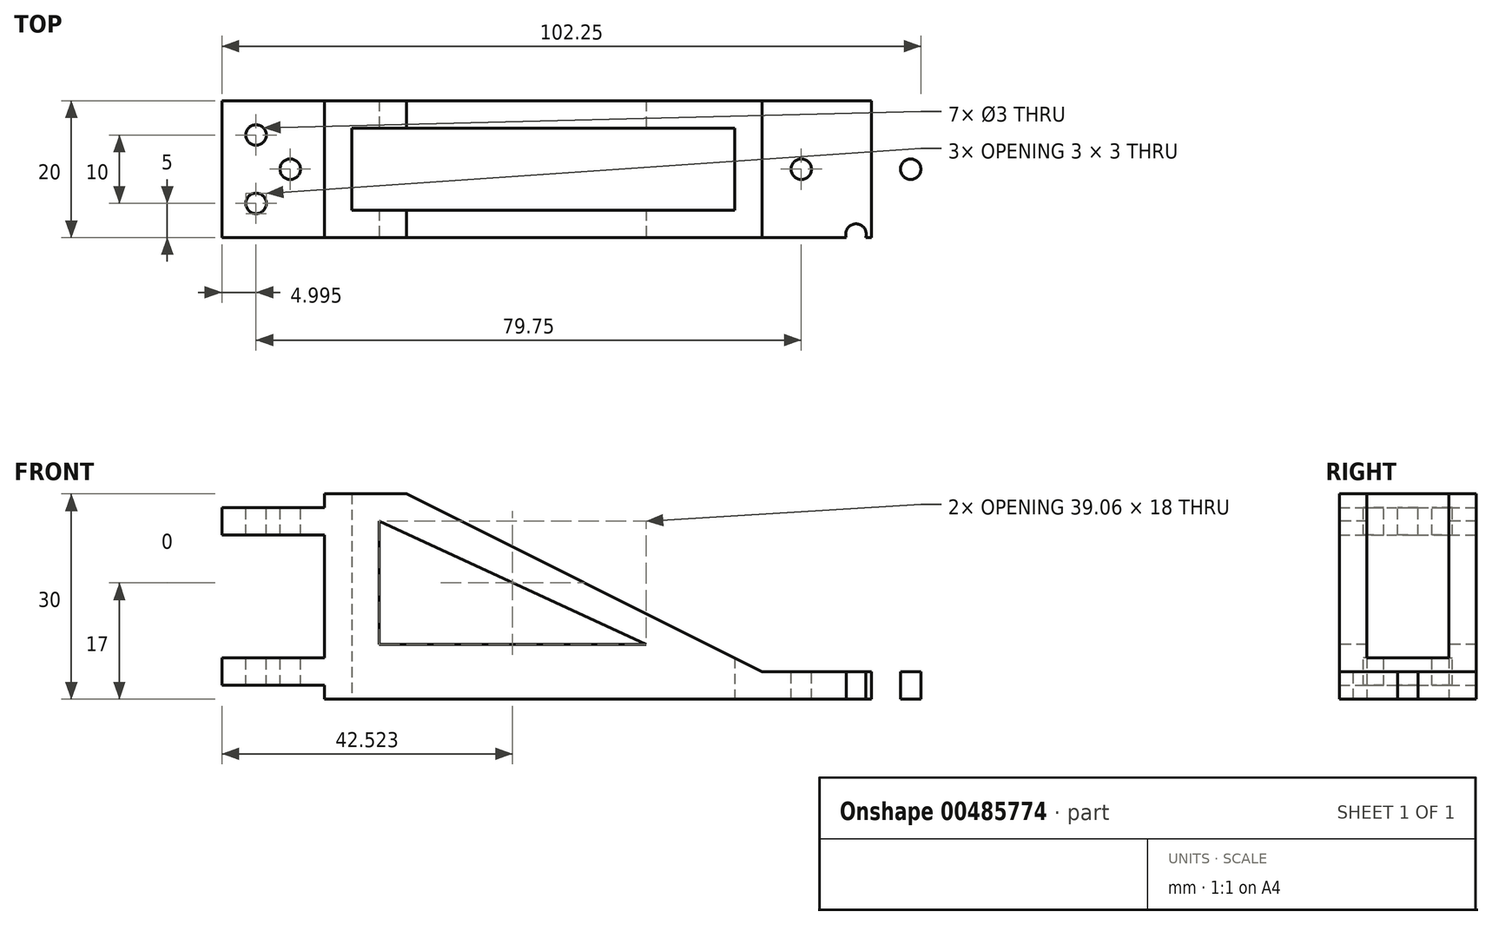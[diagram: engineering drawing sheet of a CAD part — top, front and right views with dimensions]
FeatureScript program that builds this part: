
annotation { "Feature Type Name" : "Feature", "Feature Type Description" : "" }
export const myFeature = defineFeature(function(context is Context, id is Id, definition is map)
    precondition{}
    {
        {
            var Q0;
            Q0=qCreatedBy(makeId("Front.planeOp"),FACE);
            var sketch = newSketch(context, id + "F0", { "sketchPlane" : qUnion([Q0])});
            skLineSegment(sketch, "E0", {"start": v(-74.41, 0) * mm, "end": v(5.59, 0) * mm});
            skLineSegment(sketch, "E1", {"start": v(-74.41, 0) * mm, "end": v(-74.41, 30) * mm});
            skLineSegment(sketch, "E2", {"start": v(-74.41, 30) * mm, "end": v(-70.41, 30) * mm});
            skLineSegment(sketch, "E3", {"start": v(-70.41, 30) * mm, "end": v(-70.41, 4) * mm});
            skLineSegment(sketch, "E4", {"start": v(-70.41, 4) * mm, "end": v(5.59, 4) * mm});
            skLineSegment(sketch, "E5", {"start": v(5.59, 4) * mm, "end": v(5.59, 0) * mm});
            skLineSegment(sketch, "E6.bottom", {"start": v(-74.41, 2) * mm, "end": v(-89.41, 2) * mm});
            skLineSegment(sketch, "E6.top", {"start": v(-74.41, 6) * mm, "end": v(-89.41, 6) * mm});
            skLineSegment(sketch, "E6.left", {"start": v(-74.41, 2) * mm, "end": v(-74.41, 6) * mm});
            skLineSegment(sketch, "E6.right", {"start": v(-89.41, 2) * mm, "end": v(-89.41, 6) * mm});
            skLineSegment(sketch, "E7.bottom", {"start": v(-74.41, 24) * mm, "end": v(-89.41, 24) * mm});
            skLineSegment(sketch, "E7.top", {"start": v(-74.41, 28) * mm, "end": v(-89.41, 28) * mm});
            skLineSegment(sketch, "E7.left", {"start": v(-74.41, 24) * mm, "end": v(-74.41, 28) * mm});
            skLineSegment(sketch, "E7.right", {"start": v(-89.41, 24) * mm, "end": v(-89.41, 28) * mm});
            skSolve(sketch);
        }
        {
            var Q0;
            {var subQ4=sQuery(id+"F0.wireOp",EDGE,"E0");Q0=makeQuery(id+"F0.imprint","IMPRINT",FACE,{"disambiguationData":[TD([[makeQuery(id+"F0.imprint","IMPRINT",EDGE,{"derivedFrom":subQ4}),1.0]])]});}
            var Q1;
            Q1=makeQuery(id+"F0.imprint","IMPRINT",FACE,{"disambiguationData":[TD([[makeQuery(id+"F0.imprint","IMPRINT",EDGE,{"derivedFrom":sQuery(id+"F0.wireOp",EDGE,"E7.bottom")}),-1.0]])]});
            var Q2;
            Q2=makeQuery(id+"F0.imprint","IMPRINT",FACE,{"disambiguationData":[TD([[makeQuery(id+"F0.imprint","IMPRINT",EDGE,{"derivedFrom":sQuery(id+"F0.wireOp",EDGE,"E6.bottom")}),-1.0]])]});
            extrude(context, id + "F1", {"entities" : qUnion([Q0, Q1, Q2]), "depth" : 20 * mm, "offsetDistance" : 25 * mm, "symmetric" : true});
        }
        {
            var Q0;
            Q0=makeQuery(id+"F1.opExtrude","SWEPT_EDGE",EDGE,{"disambiguationData":[OSD([sQuery(id+"F0.wireOp",EDGE,"E3"),sQuery(id+"F0.wireOp",EDGE,"E4")])]});
            chamfer(context, id + "F2", {"entities" : qUnion([Q0]), "chamferType" : ChamferType.TWO_OFFSETS, "width1" : 30 * mm, "oppositeDirection" : false, "width2" : 60 * mm, "tangentPropagation" : true});
        }
        {
            var Q0;
            Q0=makeQuery(id+"F1.opExtrude","SWEPT_FACE",FACE,{"disambiguationData":[OSD([sQuery(id+"F0.wireOp",EDGE,"E4")])]});
            var sketch = newSketch(context, id + "F3", { "sketchPlane" : qUnion([Q0])});
            skCircle(sketch, "E8", {"center": v(3.34, 0) * mm, "radius": 13.75 * mm});
            skCircle(sketch, "E9", {"center": v(-4.66, 0) * mm, "radius": 1.5 * mm});
            skCircle(sketch, "E10.MirrorC", {"center": v(11.34, 0) * mm, "radius": 1.5 * mm});
            skCircle(sketch, "E11", {"center": v(3.34, -9.5) * mm, "radius": 1.5 * mm});
            skCircle(sketch, "E12.MirrorC", {"center": v(3.34, 9.5) * mm, "radius": 1.5 * mm});
            skSolve(sketch);
        }
        {
            var Q0;
            Q0=makeQuery(id+"F3.imprint","IMPRINT",FACE,{"disambiguationData":[TD([[makeQuery(id+"F3.imprint","IMPRINT",EDGE,{"derivedFrom":sQuery(id+"F3.wireOp",EDGE,"E10.MirrorC")}),1.0]])]});
            extrude(context, id + "F4", {"entities" : qUnion([Q0]), "operationType" : NewBodyOperationType.ADD, "oppositeDirection" : true, "depth" : 4 * mm, "offsetDistance" : 25 * mm});
        }
        {
            var Q0;
            Q0=makeQuery(id+"F3.imprint","IMPRINT",FACE,{"disambiguationData":[TD([[makeQuery(id+"F3.imprint","IMPRINT",EDGE,{"derivedFrom":sQuery(id+"F3.wireOp",EDGE,"E9")}),1.0]])]});
            var Q1;
            {var subQ0=sQuery(id+"F3.wireOp",EDGE,"E11");var subQ1=makeQuery(id+"F1.opExtrude","CAP_EDGE",EDGE,{"disambiguationData":[OSD([sQuery(id+"F0.wireOp",EDGE,"E4")])],"isStart":false});var subQ2=makeQuery(id+"F3.imprint","INTERSECT",VERTEX,{"disambiguationData":[OD(0.0)],"derivedFrom":[subQ1,subQ0]});Q1=makeQuery(id+"F3.imprint","IMPRINT",FACE,{"disambiguationData":[TD([[makeQuery(id+"F3.imprint","IMPRINT",EDGE,{"disambiguationData":[TD([[subQ2,-1.0]])],"derivedFrom":subQ0}),1.0]])]});}
            var Q2;
            {var subQ0=sQuery(id+"F3.wireOp",EDGE,"E12.MirrorC");var subQ1=makeQuery(id+"F1.opExtrude","CAP_EDGE",EDGE,{"disambiguationData":[OSD([sQuery(id+"F0.wireOp",EDGE,"E4")])],"isStart":true});var subQ2=makeQuery(id+"F3.imprint","INTERSECT",VERTEX,{"disambiguationData":[OD(0.0)],"derivedFrom":[subQ1,subQ0]});Q2=makeQuery(id+"F3.imprint","IMPRINT",FACE,{"disambiguationData":[TD([[makeQuery(id+"F3.imprint","IMPRINT",EDGE,{"disambiguationData":[TD([[subQ2,-1.0]])],"derivedFrom":subQ0}),-1.0]])]});}
            extrude(context, id + "F5", {"entities" : qUnion([Q0, Q1, Q2]), "operationType" : NewBodyOperationType.REMOVE, "oppositeDirection" : true, "depth" : 4 * mm, "offsetDistance" : 25 * mm});
        }
        {
            var Q0;
            {var subQ0=sQuery(id+"F0.wireOp",EDGE,"E7.bottom");var subQ2=sQuery(id+"F0.wireOp",EDGE,"E6.right");var subQ3=sQuery(id+"F0.wireOp",EDGE,"E6.bottom");var subQ4=sQuery(id+"F0.wireOp",EDGE,"E4");var subQ5=sQuery(id+"F0.wireOp",EDGE,"E2");var subQ6=sQuery(id+"F0.wireOp",EDGE,"E6.top");var subQ7=sQuery(id+"F0.wireOp",EDGE,"E0");var subQ8=sQuery(id+"F0.wireOp",EDGE,"E1");var subQ10=sQuery(id+"F0.wireOp",EDGE,"E7.top");var subQ15=sQuery(id+"F0.wireOp",EDGE,"E5");var subQ16=sQuery(id+"F0.wireOp",EDGE,"E7.right");var subQ17=sQuery(id+"F0.wireOp",EDGE,"E3");Q0=makeQuery(id+"F4.boolean.opBoolean","SPLIT",FACE,{"disambiguationData":[TD([makeQuery(id+"F1.opExtrude","SWEPT_FACE",FACE,{"disambiguationData":[OSD([subQ5])]})])],"derivedFrom":makeQuery(id+"F1.opExtrude","CAP_FACE",FACE,{"disambiguationData":[OSD([subQ7,subQ8,subQ5,subQ17,subQ4,subQ15,subQ3,subQ6,subQ2,subQ0,subQ10,subQ16])],"isStart":false})});}
            var sketch = newSketch(context, id + "F6", { "sketchPlane" : qUnion([Q0])});
            skLineSegment(sketch, "E13", {"start": v(-66.41, 26) * mm, "end": v(-66.41, 8) * mm});
            skLineSegment(sketch, "E14", {"start": v(-66.41, 8) * mm, "end": v(-27.36, 8) * mm});
            skLineSegment(sketch, "E15", {"start": v(-27.36, 8) * mm, "end": v(-66.41, 26) * mm});
            skSolve(sketch);
        }
        {
            var Q0;
            Q0=makeQuery(id+"F6.imprint","IMPRINT",FACE,{"disambiguationData":[TD([[makeQuery(id+"F6.imprint","IMPRINT",EDGE,{"derivedFrom":sQuery(id+"F6.wireOp",EDGE,"E13")}),1.0]])]});
            extrude(context, id + "F7", {"entities" : qUnion([Q0]), "operationType" : NewBodyOperationType.REMOVE, "oppositeDirection" : true, "depth" : 20 * mm, "offsetDistance" : 25 * mm});
        }
        {
            var Q0;
            Q0=makeQuery(id+"F4.boolean.opBoolean","MERGE",FACE,{"derivedFrom":[makeQuery(id+"F1.opExtrude","SWEPT_FACE",FACE,{"disambiguationData":[OSD([sQuery(id+"F0.wireOp",EDGE,"E0")])]}),makeQuery(id+"F4.opExtrude","CAP_FACE",FACE,{"disambiguationData":[OSD([sQuery(id+"F0.wireOp",EDGE,"E4"),sQuery(id+"F0.wireOp",EDGE,"E5"),sQuery(id+"F3.wireOp",EDGE,"E8"),sQuery(id+"F3.wireOp",EDGE,"E10.MirrorC"),sQuery(id+"F3.wireOp",EDGE,"E11"),sQuery(id+"F3.wireOp",EDGE,"E12.MirrorC")])],"isStart":false})]});
            var sketch = newSketch(context, id + "F8", { "sketchPlane" : qUnion([Q0])});
            skLineSegment(sketch, "E16.bottom", {"start": v(-70.41, 6) * mm, "end": v(-14.41, 6) * mm});
            skLineSegment(sketch, "E16.top", {"start": v(-70.41, -6) * mm, "end": v(-14.41, -6) * mm});
            skLineSegment(sketch, "E16.left", {"start": v(-70.41, 6) * mm, "end": v(-70.41, -6) * mm});
            skLineSegment(sketch, "E16.right", {"start": v(-14.41, 6) * mm, "end": v(-14.41, -6) * mm});
            skSolve(sketch);
        }
        {
            var Q0;
            Q0=makeQuery(id+"F8.imprint","IMPRINT",FACE,{"disambiguationData":[TD([[makeQuery(id+"F8.imprint","IMPRINT",EDGE,{"derivedFrom":sQuery(id+"F8.wireOp",EDGE,"E16.bottom")}),-1.0]])]});
            extrude(context, id + "F9", {"entities" : qUnion([Q0]), "operationType" : NewBodyOperationType.REMOVE, "oppositeDirection" : true, "depth" : 30 * mm, "offsetDistance" : 25 * mm});
        }
        {
            var Q0;
            Q0=makeQuery(id+"F1.opExtrude","SWEPT_FACE",FACE,{"disambiguationData":[OSD([sQuery(id+"F0.wireOp",EDGE,"E7.top")])]});
            var sketch = newSketch(context, id + "F10", { "sketchPlane" : qUnion([Q0])});
            skCircle(sketch, "E17", {"center": v(-84.41, 5) * mm, "radius": 1.5 * mm});
            skCircle(sketch, "E18.MirrorC", {"center": v(-84.41, -5) * mm, "radius": 1.5 * mm});
            skCircle(sketch, "E19", {"center": v(-79.41, 0) * mm, "radius": 1.5 * mm});
            skSolve(sketch);
        }
        {
            var Q0;
            Q0 = qSketchRegion(id + "F10", true);
            extrude(context, id + "F11", {"entities" : qUnion([Q0]), "operationType" : NewBodyOperationType.REMOVE, "oppositeDirection" : true, "depth" : 26 * mm, "offsetDistance" : 25 * mm});
        }
    });
